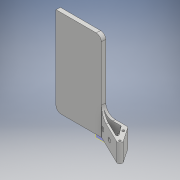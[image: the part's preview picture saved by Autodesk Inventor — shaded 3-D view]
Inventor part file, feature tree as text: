
AUTODESK INVENTOR PART (.ipt)
format: ipt  version: 2018.2 (Build 222227000, 227)  size: 233,472 bytes
history: native  units: mm
features: extrude x9, sketch x9, fillet x4, projected_geometry x2, plane x1
ambient origin geometry x8: Origin, YZ Plane, XZ Plane, XY Plane, X Axis, Y Axis, Z Axis, Center Point
bodies: Solid1 (feature_tree)
feature tree (25):
  plane  "Work Plane1"
  extrude  "Extrusion2"  Depth=28.4mm
  extrude  "Extrusion10"  Depth=3.683mm
  extrude  "Extrusion11"  Depth=4.0mm
  fillet  "Fillet5"  Radius=3.556mm
  extrude  "Extrusion12"  Depth=10.0mm
  fillet  "Fillet6"  Radius=10.0mm
  extrude  "Extrusion13"  Depth=2.0mm
  extrude  "Extrusion14"  Depth=6.0mm
  extrude  "Extrusion15"  Depth=20.0mm TaperAngle=0.0deg
  extrude  "Extrusion16"  Depth=10.0mm
  fillet  "Fillet7"  Radius=10.0mm
  extrude  "Extrusion17"  Depth=10.0mm TaperAngle=0.0deg
  fillet  "Fillet10"  Radius=10.0mm
  sketch  "Sketch2"  dims[d3=3.0mm d8=28.4mm]
  sketch  "Sketch9"  dims[d9=3.683mm d10=3.683mm]
  sketch  "Sketch10"  dims[d11=4.0mm d12=0.0mm d16=19.558mm d44=3.556mm]
  sketch  "Sketch11"  dims[d46=3.556mm d47=7.5mm d48=10.0mm d49=0.0mm]
  sketch  "Sketch12"  dims[d50=20.0mm d51=0.0mm d52=2.0mm]
  sketch  "Sketch13"  dims[d53=6.0mm d54=6.0mm]
  sketch  "Sketch14"  dims[d55=38.1mm d56=20.0mm d57=0.0mm]
  sketch  "Sketch15"  dims[d58=4.0mm d59=40.64mm d61=10.0mm d62=0.0mm]
  sketch  "Sketch16"  dims[d63=10.0mm d64=0.0mm d65=10.0mm d66=0.0mm d67=10.0mm d68=0.0mm d69=15.0mm d70=19.558mm d71=3.75mm d74=0.0mm d75=0.0mm d76=10.0mm d77=0.0mm d78=8.0mm]
  projected_geometry  "Projected Loop3"
  projected_geometry  "Projected Loop4"
